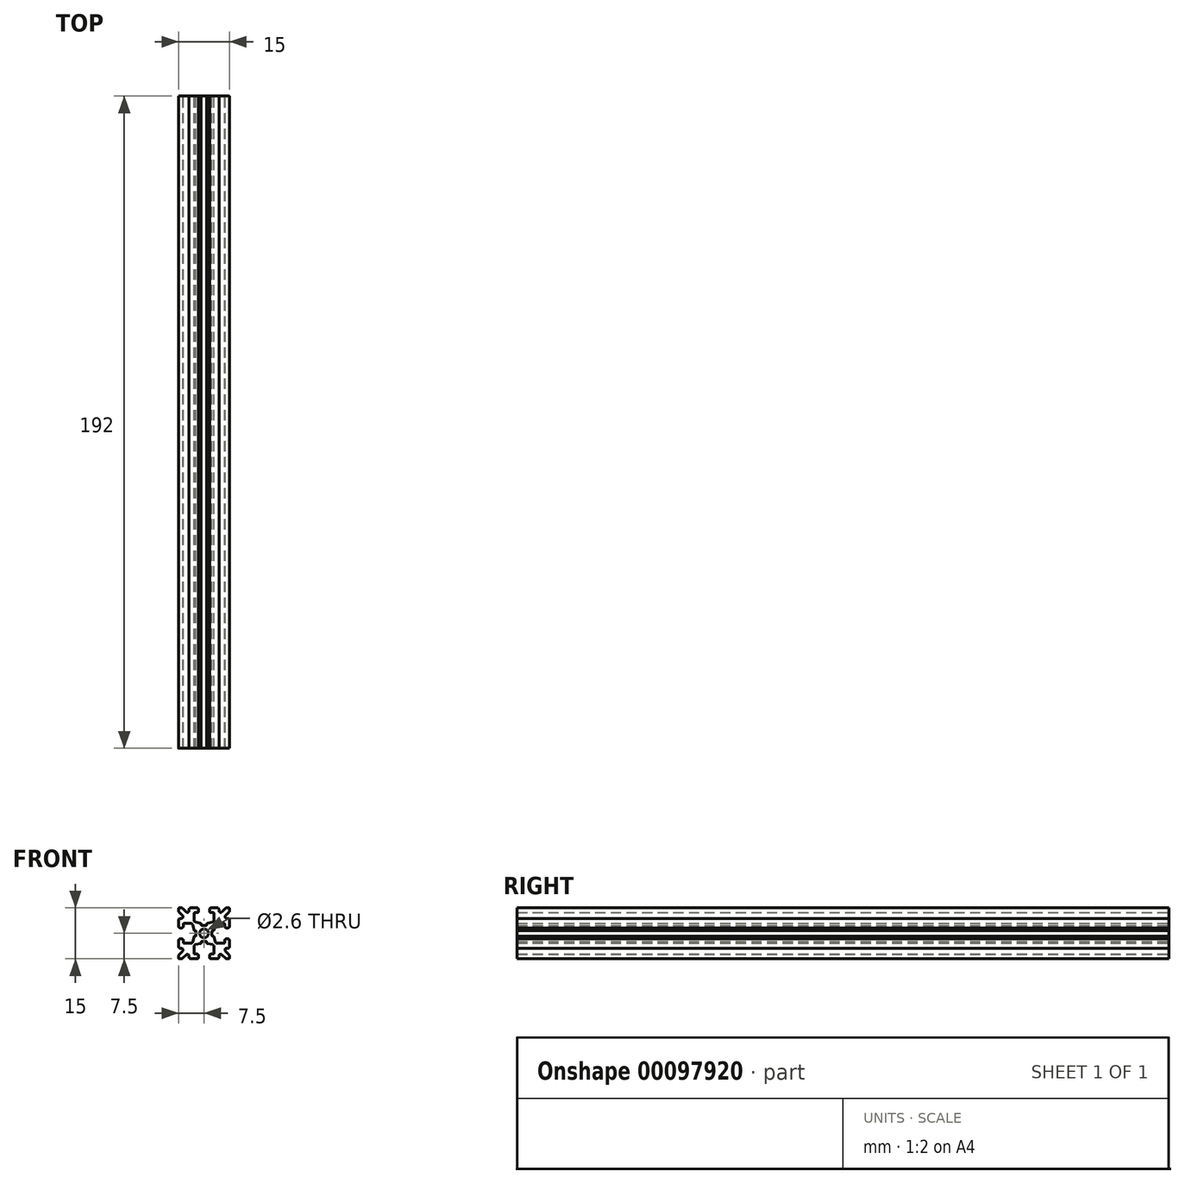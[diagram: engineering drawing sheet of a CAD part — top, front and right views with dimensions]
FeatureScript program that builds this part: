
annotation { "Feature Type Name" : "Feature", "Feature Type Description" : "" }
export const myFeature = defineFeature(function(context is Context, id is Id, definition is map)
    precondition{}
    {
        {
            var Q0;
            Q0=qCreatedBy(makeId("Front.planeOp"),FACE);
            var sketch = newSketch(context, id + "F0", { "sketchPlane" : qUnion([Q0])});
            skLineSegment(sketch, "E0.0.0", {"start": v(0.83, -2.55) * mm, "end": v(0.83, -2.77) * mm});
            skArc(sketch, "E0.0.1", {"start": v(0.83, -2.77) * mm, "mid": v(0.87, -2.9) * mm, "end": v(0.98, -2.97) * mm});
            skLineSegment(sketch, "E0.0.2", {"start": v(0.98, -2.97) * mm, "end": v(2.5, -3.31) * mm});
            skArc(sketch, "E0.0.3", {"start": v(2.5, -3.31) * mm, "mid": v(2.8, -3.49) * mm, "end": v(2.9, -3.8) * mm});
            skLineSegment(sketch, "E0.0.4", {"start": v(2.9, -3.8) * mm, "end": v(2.9, -5.9) * mm});
            skArc(sketch, "E0.0.5", {"start": v(2.9, -5.9) * mm, "mid": v(2.84, -6.04) * mm, "end": v(2.7, -6.1) * mm});
            skLineSegment(sketch, "E0.0.6", {"start": v(2.7, -6.1) * mm, "end": v(2.1, -6.1) * mm});
            skArc(sketch, "E0.0.7", {"start": v(2.1, -6.1) * mm, "mid": v(1.75, -6.25) * mm, "end": v(1.6, -6.6) * mm});
            skLineSegment(sketch, "E0.0.8", {"start": v(1.6, -6.6) * mm, "end": v(1.6, -7) * mm});
            skArc(sketch, "E0.0.9", {"start": v(1.6, -7) * mm, "mid": v(1.75, -7.35) * mm, "end": v(2.1, -7.5) * mm});
            skLineSegment(sketch, "E0.0.10", {"start": v(2.1, -7.5) * mm, "end": v(3.9, -7.5) * mm});
            skArc(sketch, "E0.0.11", {"start": v(3.9, -7.5) * mm, "mid": v(4.25, -7.35) * mm, "end": v(4.4, -7) * mm});
            skLineSegment(sketch, "E0.0.12", {"start": v(4.4, -7) * mm, "end": v(4.4, -6.67) * mm});
            skArc(sketch, "E0.0.13", {"start": v(4.4, -6.67) * mm, "mid": v(4.7, -6.2) * mm, "end": v(5.25, -6.31) * mm});
            skLineSegment(sketch, "E0.0.14", {"start": v(5.25, -6.31) * mm, "end": v(6.3, -7.35) * mm});
            skArc(sketch, "E0.0.15", {"start": v(6.3, -7.35) * mm, "mid": v(6.46, -7.46) * mm, "end": v(6.65, -7.5) * mm});
            skLineSegment(sketch, "E0.0.16", {"start": v(6.65, -7.5) * mm, "end": v(7.25, -7.5) * mm});
            skArc(sketch, "E0.0.17", {"start": v(7.25, -7.5) * mm, "mid": v(7.43, -7.43) * mm, "end": v(7.5, -7.25) * mm});
            skLineSegment(sketch, "E0.0.18", {"start": v(7.5, -7.25) * mm, "end": v(7.5, -6.65) * mm});
            skArc(sketch, "E0.0.19", {"start": v(7.5, -6.65) * mm, "mid": v(7.46, -6.46) * mm, "end": v(7.35, -6.3) * mm});
            skLineSegment(sketch, "E0.0.20", {"start": v(7.35, -6.3) * mm, "end": v(6.31, -5.25) * mm});
            skArc(sketch, "E0.0.21", {"start": v(6.31, -5.25) * mm, "mid": v(6.2, -4.7) * mm, "end": v(6.67, -4.4) * mm});
            skLineSegment(sketch, "E0.0.22", {"start": v(6.67, -4.4) * mm, "end": v(7, -4.4) * mm});
            skArc(sketch, "E0.0.23", {"start": v(7, -4.4) * mm, "mid": v(7.35, -4.25) * mm, "end": v(7.5, -3.9) * mm});
            skLineSegment(sketch, "E0.0.24", {"start": v(7.5, -3.9) * mm, "end": v(7.5, -2.1) * mm});
            skArc(sketch, "E0.0.25", {"start": v(7.5, -2.1) * mm, "mid": v(7.35, -1.75) * mm, "end": v(7, -1.6) * mm});
            skLineSegment(sketch, "E0.0.26", {"start": v(7, -1.6) * mm, "end": v(6.6, -1.6) * mm});
            skArc(sketch, "E0.0.27", {"start": v(6.6, -1.6) * mm, "mid": v(6.25, -1.75) * mm, "end": v(6.1, -2.1) * mm});
            skLineSegment(sketch, "E0.0.28", {"start": v(6.1, -2.1) * mm, "end": v(6.1, -2.7) * mm});
            skArc(sketch, "E0.0.29", {"start": v(6.1, -2.7) * mm, "mid": v(6.04, -2.84) * mm, "end": v(5.9, -2.9) * mm});
            skLineSegment(sketch, "E0.0.30", {"start": v(5.9, -2.9) * mm, "end": v(3.8, -2.9) * mm});
            skArc(sketch, "E0.0.31", {"start": v(3.8, -2.9) * mm, "mid": v(3.49, -2.8) * mm, "end": v(3.31, -2.5) * mm});
            skLineSegment(sketch, "E0.0.32", {"start": v(3.31, -2.5) * mm, "end": v(2.97, -0.98) * mm});
            skArc(sketch, "E0.0.33", {"start": v(2.97, -0.98) * mm, "mid": v(2.9, -0.87) * mm, "end": v(2.77, -0.83) * mm});
            skLineSegment(sketch, "E0.0.34", {"start": v(2.77, -0.83) * mm, "end": v(2.55, -0.83) * mm});
            skArc(sketch, "E0.0.35", {"start": v(2.55, -0.83) * mm, "mid": v(2.4, -0.77) * mm, "end": v(2.35, -0.63) * mm});
            skLineSegment(sketch, "E0.0.36", {"start": v(2.35, -0.63) * mm, "end": v(2.35, 0.63) * mm});
            skArc(sketch, "E0.0.37", {"start": v(2.35, 0.63) * mm, "mid": v(2.4, 0.77) * mm, "end": v(2.55, 0.83) * mm});
            skLineSegment(sketch, "E0.0.38", {"start": v(2.55, 0.83) * mm, "end": v(2.77, 0.83) * mm});
            skArc(sketch, "E0.0.39", {"start": v(2.77, 0.83) * mm, "mid": v(2.9, 0.87) * mm, "end": v(2.97, 0.98) * mm});
            skLineSegment(sketch, "E0.0.40", {"start": v(2.97, 0.98) * mm, "end": v(3.31, 2.5) * mm});
            skArc(sketch, "E0.0.41", {"start": v(3.31, 2.5) * mm, "mid": v(3.49, 2.8) * mm, "end": v(3.8, 2.9) * mm});
            skLineSegment(sketch, "E0.0.42", {"start": v(3.8, 2.9) * mm, "end": v(5.9, 2.9) * mm});
            skArc(sketch, "E0.0.43", {"start": v(5.9, 2.9) * mm, "mid": v(6.04, 2.84) * mm, "end": v(6.1, 2.7) * mm});
            skLineSegment(sketch, "E0.0.44", {"start": v(6.1, 2.7) * mm, "end": v(6.1, 2.1) * mm});
            skArc(sketch, "E0.0.45", {"start": v(6.1, 2.1) * mm, "mid": v(6.25, 1.75) * mm, "end": v(6.6, 1.6) * mm});
            skLineSegment(sketch, "E0.0.46", {"start": v(6.6, 1.6) * mm, "end": v(7, 1.6) * mm});
            skArc(sketch, "E0.0.47", {"start": v(7, 1.6) * mm, "mid": v(7.35, 1.75) * mm, "end": v(7.5, 2.1) * mm});
            skLineSegment(sketch, "E0.0.48", {"start": v(7.5, 2.1) * mm, "end": v(7.5, 3.9) * mm});
            skArc(sketch, "E0.0.49", {"start": v(7.5, 3.9) * mm, "mid": v(7.35, 4.25) * mm, "end": v(7, 4.4) * mm});
            skLineSegment(sketch, "E0.0.50", {"start": v(7, 4.4) * mm, "end": v(6.67, 4.4) * mm});
            skArc(sketch, "E0.0.51", {"start": v(6.67, 4.4) * mm, "mid": v(6.2, 4.7) * mm, "end": v(6.31, 5.25) * mm});
            skLineSegment(sketch, "E0.0.52", {"start": v(6.31, 5.25) * mm, "end": v(7.35, 6.3) * mm});
            skArc(sketch, "E0.0.53", {"start": v(7.35, 6.3) * mm, "mid": v(7.46, 6.46) * mm, "end": v(7.5, 6.65) * mm});
            skLineSegment(sketch, "E0.0.54", {"start": v(7.5, 6.65) * mm, "end": v(7.5, 7.25) * mm});
            skArc(sketch, "E0.0.55", {"start": v(7.5, 7.25) * mm, "mid": v(7.43, 7.43) * mm, "end": v(7.25, 7.5) * mm});
            skLineSegment(sketch, "E0.0.56", {"start": v(7.25, 7.5) * mm, "end": v(6.65, 7.5) * mm});
            skArc(sketch, "E0.0.57", {"start": v(6.65, 7.5) * mm, "mid": v(6.46, 7.46) * mm, "end": v(6.3, 7.35) * mm});
            skLineSegment(sketch, "E0.0.58", {"start": v(6.3, 7.35) * mm, "end": v(5.25, 6.31) * mm});
            skArc(sketch, "E0.0.59", {"start": v(5.25, 6.31) * mm, "mid": v(4.7, 6.2) * mm, "end": v(4.4, 6.67) * mm});
            skLineSegment(sketch, "E0.0.60", {"start": v(4.4, 6.67) * mm, "end": v(4.4, 7) * mm});
            skArc(sketch, "E0.0.61", {"start": v(4.4, 7) * mm, "mid": v(4.25, 7.35) * mm, "end": v(3.9, 7.5) * mm});
            skLineSegment(sketch, "E0.0.62", {"start": v(3.9, 7.5) * mm, "end": v(2.1, 7.5) * mm});
            skArc(sketch, "E0.0.63", {"start": v(2.1, 7.5) * mm, "mid": v(1.75, 7.35) * mm, "end": v(1.6, 7) * mm});
            skLineSegment(sketch, "E0.0.64", {"start": v(1.6, 7) * mm, "end": v(1.6, 6.6) * mm});
            skArc(sketch, "E0.0.65", {"start": v(1.6, 6.6) * mm, "mid": v(1.75, 6.25) * mm, "end": v(2.1, 6.1) * mm});
            skLineSegment(sketch, "E0.0.66", {"start": v(2.1, 6.1) * mm, "end": v(2.7, 6.1) * mm});
            skArc(sketch, "E0.0.67", {"start": v(2.7, 6.1) * mm, "mid": v(2.84, 6.04) * mm, "end": v(2.9, 5.9) * mm});
            skLineSegment(sketch, "E0.0.68", {"start": v(2.9, 5.9) * mm, "end": v(2.9, 3.8) * mm});
            skArc(sketch, "E0.0.69", {"start": v(2.9, 3.8) * mm, "mid": v(2.8, 3.49) * mm, "end": v(2.5, 3.31) * mm});
            skLineSegment(sketch, "E0.0.70", {"start": v(2.5, 3.31) * mm, "end": v(0.98, 2.97) * mm});
            skArc(sketch, "E0.0.71", {"start": v(0.98, 2.97) * mm, "mid": v(0.87, 2.9) * mm, "end": v(0.83, 2.77) * mm});
            skLineSegment(sketch, "E0.0.72", {"start": v(0.83, 2.77) * mm, "end": v(0.83, 2.55) * mm});
            skArc(sketch, "E0.0.73", {"start": v(0.83, 2.55) * mm, "mid": v(0.77, 2.4) * mm, "end": v(0.63, 2.35) * mm});
            skLineSegment(sketch, "E0.0.74", {"start": v(0.63, 2.35) * mm, "end": v(-0.63, 2.35) * mm});
            skArc(sketch, "E0.0.75", {"start": v(-0.63, 2.35) * mm, "mid": v(-0.77, 2.4) * mm, "end": v(-0.83, 2.55) * mm});
            skLineSegment(sketch, "E0.0.76", {"start": v(-0.83, 2.55) * mm, "end": v(-0.83, 2.77) * mm});
            skArc(sketch, "E0.0.77", {"start": v(-0.83, 2.77) * mm, "mid": v(-0.87, 2.9) * mm, "end": v(-0.98, 2.97) * mm});
            skLineSegment(sketch, "E0.0.78", {"start": v(-0.98, 2.97) * mm, "end": v(-2.5, 3.31) * mm});
            skArc(sketch, "E0.0.79", {"start": v(-2.5, 3.31) * mm, "mid": v(-2.8, 3.49) * mm, "end": v(-2.9, 3.8) * mm});
            skLineSegment(sketch, "E0.0.80", {"start": v(-2.9, 3.8) * mm, "end": v(-2.9, 5.9) * mm});
            skArc(sketch, "E0.0.81", {"start": v(-2.9, 5.9) * mm, "mid": v(-2.84, 6.04) * mm, "end": v(-2.7, 6.1) * mm});
            skLineSegment(sketch, "E0.0.82", {"start": v(-2.7, 6.1) * mm, "end": v(-2.1, 6.1) * mm});
            skArc(sketch, "E0.0.83", {"start": v(-2.1, 6.1) * mm, "mid": v(-1.75, 6.25) * mm, "end": v(-1.6, 6.6) * mm});
            skLineSegment(sketch, "E0.0.84", {"start": v(-1.6, 6.6) * mm, "end": v(-1.6, 7) * mm});
            skArc(sketch, "E0.0.85", {"start": v(-1.6, 7) * mm, "mid": v(-1.75, 7.35) * mm, "end": v(-2.1, 7.5) * mm});
            skLineSegment(sketch, "E0.0.86", {"start": v(-2.1, 7.5) * mm, "end": v(-3.9, 7.5) * mm});
            skArc(sketch, "E0.0.87", {"start": v(-3.9, 7.5) * mm, "mid": v(-4.25, 7.35) * mm, "end": v(-4.4, 7) * mm});
            skLineSegment(sketch, "E0.0.88", {"start": v(-4.4, 7) * mm, "end": v(-4.4, 6.67) * mm});
            skArc(sketch, "E0.0.89", {"start": v(-4.4, 6.67) * mm, "mid": v(-4.7, 6.2) * mm, "end": v(-5.25, 6.31) * mm});
            skLineSegment(sketch, "E0.0.90", {"start": v(-5.25, 6.31) * mm, "end": v(-6.3, 7.35) * mm});
            skArc(sketch, "E0.0.91", {"start": v(-6.3, 7.35) * mm, "mid": v(-6.46, 7.46) * mm, "end": v(-6.65, 7.5) * mm});
            skLineSegment(sketch, "E0.0.92", {"start": v(-6.65, 7.5) * mm, "end": v(-7.25, 7.5) * mm});
            skArc(sketch, "E0.0.93", {"start": v(-7.25, 7.5) * mm, "mid": v(-7.43, 7.43) * mm, "end": v(-7.5, 7.25) * mm});
            skLineSegment(sketch, "E0.0.94", {"start": v(-7.5, 7.25) * mm, "end": v(-7.5, 6.65) * mm});
            skArc(sketch, "E0.0.95", {"start": v(-7.5, 6.65) * mm, "mid": v(-7.46, 6.46) * mm, "end": v(-7.35, 6.3) * mm});
            skLineSegment(sketch, "E0.0.96", {"start": v(-7.35, 6.3) * mm, "end": v(-6.31, 5.25) * mm});
            skArc(sketch, "E0.0.97", {"start": v(-6.31, 5.25) * mm, "mid": v(-6.2, 4.7) * mm, "end": v(-6.67, 4.4) * mm});
            skLineSegment(sketch, "E0.0.98", {"start": v(-6.67, 4.4) * mm, "end": v(-7, 4.4) * mm});
            skArc(sketch, "E0.0.99", {"start": v(-7, 4.4) * mm, "mid": v(-7.35, 4.25) * mm, "end": v(-7.5, 3.9) * mm});
            skLineSegment(sketch, "E0.0.100", {"start": v(-7.5, 3.9) * mm, "end": v(-7.5, 2.1) * mm});
            skArc(sketch, "E0.0.101", {"start": v(-7.5, 2.1) * mm, "mid": v(-7.35, 1.75) * mm, "end": v(-7, 1.6) * mm});
            skLineSegment(sketch, "E0.0.102", {"start": v(-7, 1.6) * mm, "end": v(-6.6, 1.6) * mm});
            skArc(sketch, "E0.0.103", {"start": v(-6.6, 1.6) * mm, "mid": v(-6.25, 1.75) * mm, "end": v(-6.1, 2.1) * mm});
            skLineSegment(sketch, "E0.0.104", {"start": v(-6.1, 2.1) * mm, "end": v(-6.1, 2.7) * mm});
            skArc(sketch, "E0.0.105", {"start": v(-6.1, 2.7) * mm, "mid": v(-6.04, 2.84) * mm, "end": v(-5.9, 2.9) * mm});
            skLineSegment(sketch, "E0.0.106", {"start": v(-5.9, 2.9) * mm, "end": v(-3.8, 2.9) * mm});
            skArc(sketch, "E0.0.107", {"start": v(-3.8, 2.9) * mm, "mid": v(-3.49, 2.8) * mm, "end": v(-3.31, 2.5) * mm});
            skLineSegment(sketch, "E0.0.108", {"start": v(-3.31, 2.5) * mm, "end": v(-2.97, 0.98) * mm});
            skArc(sketch, "E0.0.109", {"start": v(-2.97, 0.98) * mm, "mid": v(-2.9, 0.87) * mm, "end": v(-2.77, 0.83) * mm});
            skLineSegment(sketch, "E0.0.110", {"start": v(-2.77, 0.83) * mm, "end": v(-2.55, 0.83) * mm});
            skArc(sketch, "E0.0.111", {"start": v(-2.55, 0.83) * mm, "mid": v(-2.4, 0.77) * mm, "end": v(-2.35, 0.63) * mm});
            skLineSegment(sketch, "E0.0.112", {"start": v(-2.35, 0.63) * mm, "end": v(-2.35, -0.63) * mm});
            skArc(sketch, "E0.0.113", {"start": v(-2.35, -0.63) * mm, "mid": v(-2.4, -0.77) * mm, "end": v(-2.55, -0.83) * mm});
            skLineSegment(sketch, "E0.0.114", {"start": v(-2.55, -0.83) * mm, "end": v(-2.77, -0.83) * mm});
            skArc(sketch, "E0.0.115", {"start": v(-2.77, -0.83) * mm, "mid": v(-2.9, -0.87) * mm, "end": v(-2.97, -0.98) * mm});
            skLineSegment(sketch, "E0.0.116", {"start": v(-2.97, -0.98) * mm, "end": v(-3.31, -2.5) * mm});
            skArc(sketch, "E0.0.117", {"start": v(-3.31, -2.5) * mm, "mid": v(-3.49, -2.8) * mm, "end": v(-3.8, -2.9) * mm});
            skLineSegment(sketch, "E0.0.118", {"start": v(-3.8, -2.9) * mm, "end": v(-5.9, -2.9) * mm});
            skArc(sketch, "E0.0.119", {"start": v(-5.9, -2.9) * mm, "mid": v(-6.04, -2.84) * mm, "end": v(-6.1, -2.7) * mm});
            skLineSegment(sketch, "E0.0.120", {"start": v(-6.1, -2.7) * mm, "end": v(-6.1, -2.1) * mm});
            skArc(sketch, "E0.0.121", {"start": v(-6.1, -2.1) * mm, "mid": v(-6.25, -1.75) * mm, "end": v(-6.6, -1.6) * mm});
            skLineSegment(sketch, "E0.0.122", {"start": v(-6.6, -1.6) * mm, "end": v(-7, -1.6) * mm});
            skArc(sketch, "E0.0.123", {"start": v(-7, -1.6) * mm, "mid": v(-7.35, -1.75) * mm, "end": v(-7.5, -2.1) * mm});
            skLineSegment(sketch, "E0.0.124", {"start": v(-7.5, -2.1) * mm, "end": v(-7.5, -3.9) * mm});
            skArc(sketch, "E0.0.125", {"start": v(-7.5, -3.9) * mm, "mid": v(-7.35, -4.25) * mm, "end": v(-7, -4.4) * mm});
            skLineSegment(sketch, "E0.0.126", {"start": v(-7, -4.4) * mm, "end": v(-6.67, -4.4) * mm});
            skArc(sketch, "E0.0.127", {"start": v(-6.67, -4.4) * mm, "mid": v(-6.2, -4.7) * mm, "end": v(-6.31, -5.25) * mm});
            skLineSegment(sketch, "E0.0.128", {"start": v(-6.31, -5.25) * mm, "end": v(-7.35, -6.3) * mm});
            skArc(sketch, "E0.0.129", {"start": v(-7.35, -6.3) * mm, "mid": v(-7.46, -6.46) * mm, "end": v(-7.5, -6.65) * mm});
            skLineSegment(sketch, "E0.0.130", {"start": v(-7.5, -6.65) * mm, "end": v(-7.5, -7.25) * mm});
            skArc(sketch, "E0.0.131", {"start": v(-7.5, -7.25) * mm, "mid": v(-7.43, -7.43) * mm, "end": v(-7.25, -7.5) * mm});
            skLineSegment(sketch, "E0.0.132", {"start": v(-7.25, -7.5) * mm, "end": v(-6.65, -7.5) * mm});
            skArc(sketch, "E0.0.133", {"start": v(-6.65, -7.5) * mm, "mid": v(-6.46, -7.46) * mm, "end": v(-6.3, -7.35) * mm});
            skLineSegment(sketch, "E0.0.134", {"start": v(-6.3, -7.35) * mm, "end": v(-5.25, -6.31) * mm});
            skArc(sketch, "E0.0.135", {"start": v(-5.25, -6.31) * mm, "mid": v(-4.7, -6.2) * mm, "end": v(-4.4, -6.67) * mm});
            skLineSegment(sketch, "E0.0.136", {"start": v(-4.4, -6.67) * mm, "end": v(-4.4, -7) * mm});
            skArc(sketch, "E0.0.137", {"start": v(-4.4, -7) * mm, "mid": v(-4.25, -7.35) * mm, "end": v(-3.9, -7.5) * mm});
            skLineSegment(sketch, "E0.0.138", {"start": v(-3.9, -7.5) * mm, "end": v(-2.1, -7.5) * mm});
            skArc(sketch, "E0.0.139", {"start": v(-2.1, -7.5) * mm, "mid": v(-1.75, -7.35) * mm, "end": v(-1.6, -7) * mm});
            skLineSegment(sketch, "E0.0.140", {"start": v(-1.6, -7) * mm, "end": v(-1.6, -6.6) * mm});
            skArc(sketch, "E0.0.141", {"start": v(-1.6, -6.6) * mm, "mid": v(-1.75, -6.25) * mm, "end": v(-2.1, -6.1) * mm});
            skLineSegment(sketch, "E0.0.142", {"start": v(-2.1, -6.1) * mm, "end": v(-2.7, -6.1) * mm});
            skArc(sketch, "E0.0.143", {"start": v(-2.7, -6.1) * mm, "mid": v(-2.84, -6.04) * mm, "end": v(-2.9, -5.9) * mm});
            skLineSegment(sketch, "E0.0.144", {"start": v(-2.9, -5.9) * mm, "end": v(-2.9, -3.8) * mm});
            skArc(sketch, "E0.0.145", {"start": v(-2.9, -3.8) * mm, "mid": v(-2.8, -3.49) * mm, "end": v(-2.5, -3.31) * mm});
            skLineSegment(sketch, "E0.0.146", {"start": v(-2.5, -3.31) * mm, "end": v(-0.98, -2.97) * mm});
            skArc(sketch, "E0.0.147", {"start": v(-0.98, -2.97) * mm, "mid": v(-0.87, -2.9) * mm, "end": v(-0.83, -2.77) * mm});
            skLineSegment(sketch, "E0.0.148", {"start": v(-0.83, -2.77) * mm, "end": v(-0.83, -2.55) * mm});
            skArc(sketch, "E0.0.149", {"start": v(-0.83, -2.55) * mm, "mid": v(-0.77, -2.4) * mm, "end": v(-0.63, -2.35) * mm});
            skLineSegment(sketch, "E0.0.150", {"start": v(-0.63, -2.35) * mm, "end": v(0.63, -2.35) * mm});
            skArc(sketch, "E0.0.151", {"start": v(0.63, -2.35) * mm, "mid": v(0.77, -2.4) * mm, "end": v(0.83, -2.55) * mm});
            skPoint(sketch, "E1", {"position": v(0, 0) * mm});
            skPoint(sketch, "E1.positionSnap0", {"position": v(0, 2.35) * mm});
            skPoint(sketch, "E1.positionSnap1", {"position": v(2.35, 0) * mm});
            skCircle(sketch, "E2", {"center": v(0, 0) * mm, "radius": 1.3 * mm});
            skSolve(sketch);
        }
        {
            var Q0;
            Q0=makeQuery(id+"F0.imprint","IMPRINT",FACE,{"disambiguationData":[TD([[makeQuery(id+"F0.imprint","IMPRINT",EDGE,{"derivedFrom":sQuery(id+"F0.wireOp",EDGE,"E0.0.0")}),1.0]])]});
            extrude(context, id + "F1", {"entities" : qUnion([Q0]), "endBound" : BoundingType.SYMMETRIC, "depth" : 192 * mm});
        }
    });
